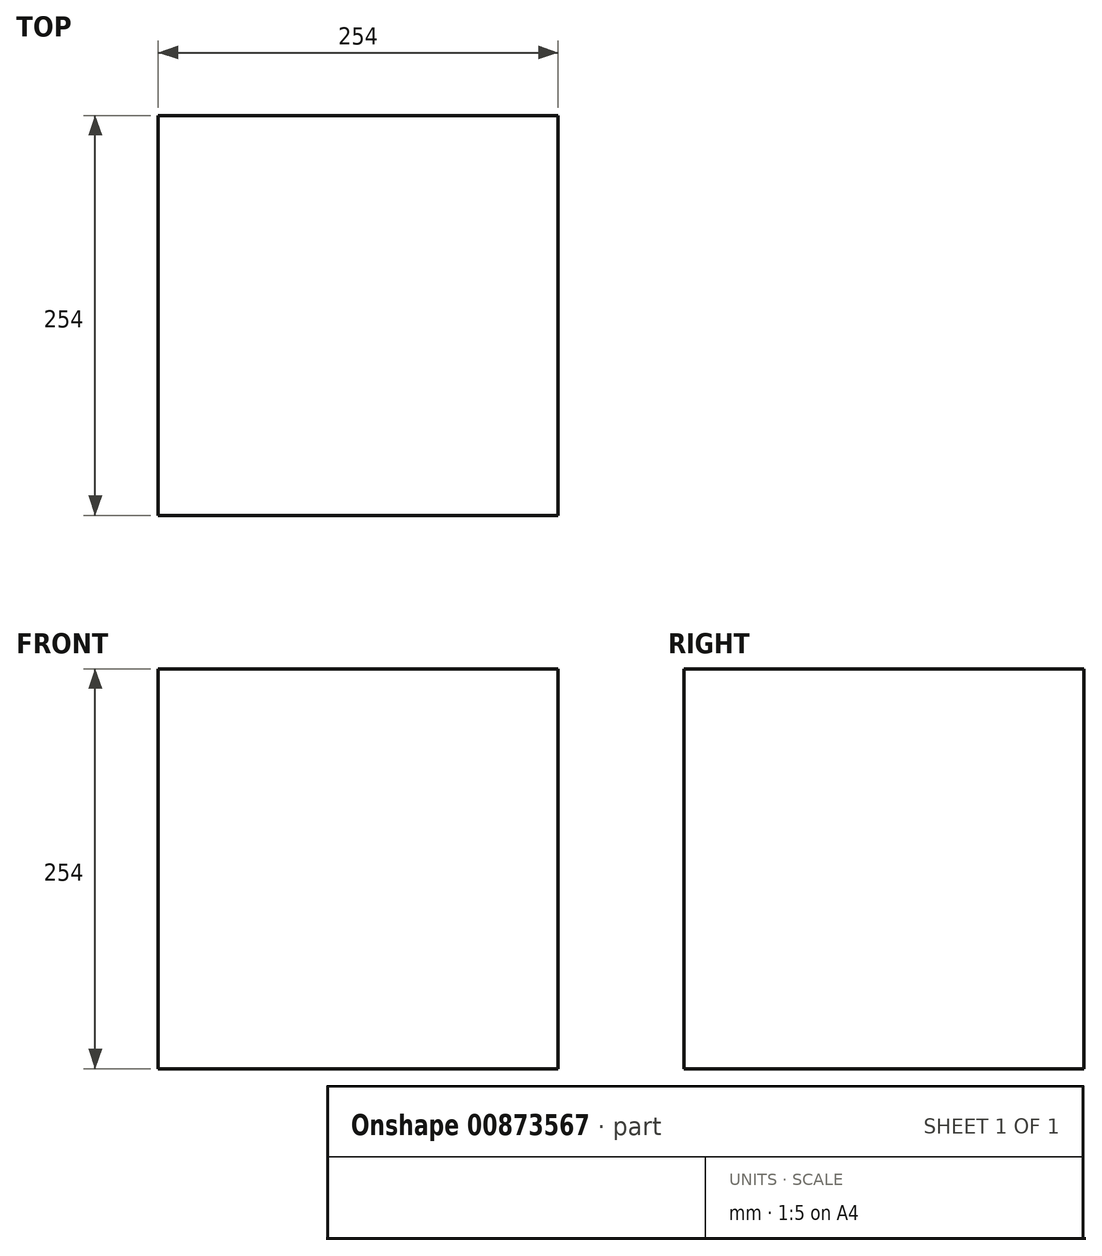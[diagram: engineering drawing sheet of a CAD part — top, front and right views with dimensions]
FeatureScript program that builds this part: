
annotation { "Feature Type Name" : "Feature", "Feature Type Description" : "" }
export const myFeature = defineFeature(function(context is Context, id is Id, definition is map)
    precondition{}
    {
        {
            var Q0;
            Q0=qCreatedBy(makeId("Top.planeOp"),FACE);
            var sketch = newSketch(context, id + "F0", { "sketchPlane" : qUnion([Q0])});
            skLineSegment(sketch, "E0.bottom", {"start": v(-127, -127) * mm, "end": v(127, -127) * mm});
            skLineSegment(sketch, "E0.top", {"start": v(-127, 127) * mm, "end": v(127, 127) * mm});
            skLineSegment(sketch, "E0.left", {"start": v(-127, -127) * mm, "end": v(-127, 127) * mm});
            skLineSegment(sketch, "E0.right", {"start": v(127, -127) * mm, "end": v(127, 127) * mm});
            skPoint(sketch, "E0.middle", {"position": v(0, 0) * mm});
            skSolve(sketch);
        }
        {
            var Q0;
            Q0 = qSketchRegion(id + "F0", true);
            var Q1;
            Q1=makeQuery(id+"F0.imprint","IMPRINT",FACE,{"disambiguationData":[TD([[makeQuery(id+"F0.imprint","IMPRINT",EDGE,{"derivedFrom":sQuery(id+"F0.wireOp",EDGE,"E0.bottom")}),1.0]])]});
            extrude(context, id + "F1", {"entities" : qUnion([Q0, Q1]), "depth" : 254 * mm, "offsetDistance" : 25.4 * mm});
        }
    });
